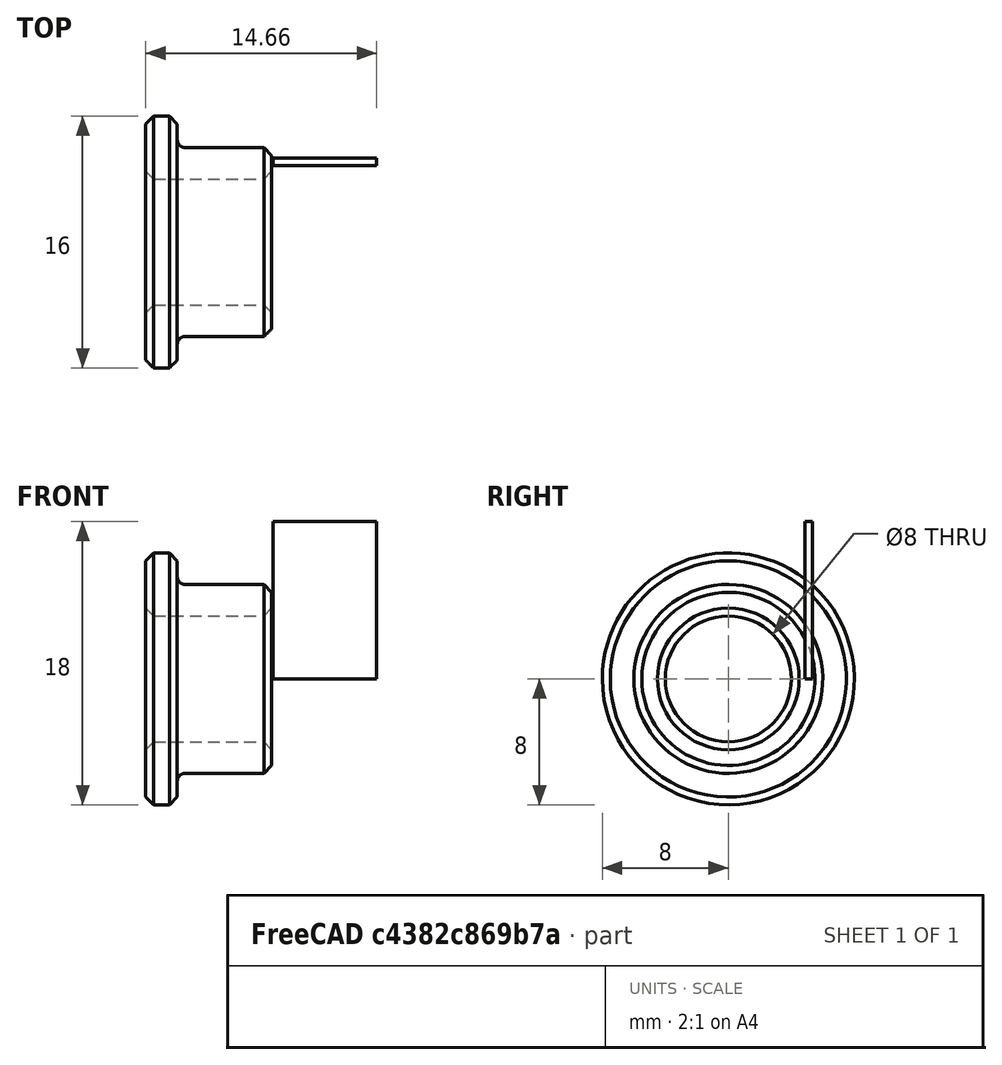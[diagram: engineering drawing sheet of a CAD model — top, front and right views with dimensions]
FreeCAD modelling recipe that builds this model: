
FCSTD DOCUMENT  (FreeCAD 0.15R4671 (Git))
Label: Coussinet lub
License: All rights reserved
LicenseURL: http://en.wikipedia.org/wiki/All_rights_reserved
objects: Part::Feature×1, Sketcher::SketchObject×1, PartDesign::Pad×1
note: 4 computed .brp shape members not serialized (recipe doc carries the construction recipe); baked Part::Feature solids carry a one-line shape summary decoded from their .brp

FEATURE [Part::Feature] Part__Feature  label="_michaud_chailly_C2-151-8-128"
  shape: bbox 8 x 16 x 16 mm, 12 faces (baked)
FEATURE [Sketcher::SketchObject] Sketch
  sketch-geometry (4):
    g0: LineSegment StartX=6.08288 StartY=5.34017 StartZ=0 EndX=12.6551 EndY=5.34017 EndZ=0
    g1: LineSegment StartX=12.6551 StartY=5.34017 StartZ=0 EndX=12.6551 EndY=4.87073 EndZ=0
    g2: LineSegment StartX=12.6551 StartY=4.87073 StartZ=0 EndX=6.08288 EndY=4.87073 EndZ=0
    g3: LineSegment StartX=6.08288 StartY=4.87073 StartZ=0 EndX=6.08288 EndY=5.34017 EndZ=0
  constraints (8):
    c: Horizontal(g0)
    c: Coincident(g0,g1)
    c: Vertical(g1)
    c: Coincident(g1,g2)
    c: Horizontal(g2)
    c: Coincident(g2,g3)
    c: Coincident(g3,g0)
    c: Vertical(g3)
FEATURE [PartDesign::Pad] Pad
  Length = 10
  Length2 = 100
  Sketch = -> Sketch
  Type = 0
